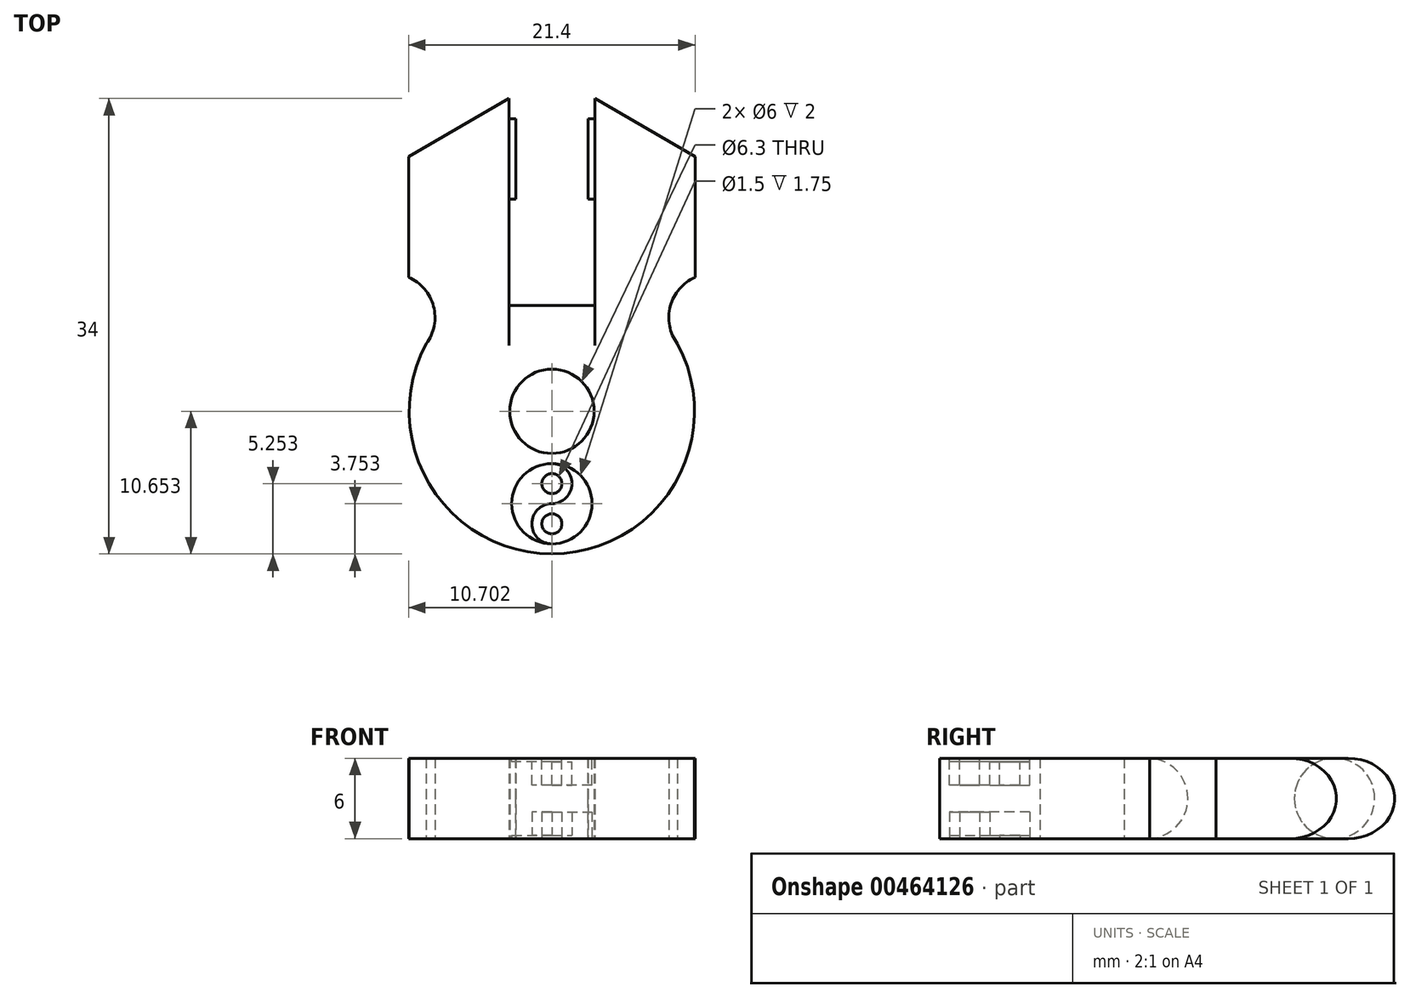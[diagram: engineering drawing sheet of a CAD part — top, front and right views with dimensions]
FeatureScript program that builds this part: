
annotation { "Feature Type Name" : "Feature", "Feature Type Description" : "" }
export const myFeature = defineFeature(function(context is Context, id is Id, definition is map)
    precondition{}
    {
        {
            var Q0;
            Q0=qCreatedBy(makeId("Top.planeOp"),FACE);
            var sketch = newSketch(context, id + "F0", { "sketchPlane" : qUnion([Q0])});
            skCircle(sketch, "E0", {"center": v(-10.56, -6.9) * mm, "radius": 10.65 * mm});
            skCircle(sketch, "E1", {"center": v(-10.56, -6.9) * mm, "radius": 3.15 * mm});
            skLineSegment(sketch, "E2", {"start": v(-10.56, -6.9) * mm, "end": v(-10.56, 3.74) * mm});
            skLineSegment(sketch, "E3", {"start": v(-13.76, 1.2) * mm, "end": v(-13.76, 16.44) * mm});
            skLineSegment(sketch, "E4", {"start": v(-7.36, 1.2) * mm, "end": v(-7.36, 16.44) * mm});
            skLineSegment(sketch, "E5", {"start": v(-7.36, 16.44) * mm, "end": v(0.14, 12.1) * mm});
            skLineSegment(sketch, "E6", {"start": v(-13.76, 16.44) * mm, "end": v(-21.26, 12.1) * mm});
            skLineSegment(sketch, "E7", {"start": v(-21.26, 12.1) * mm, "end": v(-21.26, 3.1) * mm});
            skLineSegment(sketch, "E8", {"start": v(0.14, 12.1) * mm, "end": v(0.14, 3.1) * mm});
            skLineSegment(sketch, "E9", {"start": v(-21.26, 12.1) * mm, "end": v(-21.26, 16.44) * mm});
            skLineSegment(sketch, "E10", {"start": v(-21.26, 16.44) * mm, "end": v(-13.76, 16.44) * mm});
            skArc(sketch, "E11", {"start": v(-19.94, -1.86) * mm, "mid": v(-19.4, 0.93) * mm, "end": v(-21.26, 3.1) * mm});
            skArc(sketch, "E12", {"start": v(0.14, 3.1) * mm, "mid": v(-1.72, 0.93) * mm, "end": v(-1.18, -1.86) * mm});
            skLineSegment(sketch, "E13", {"start": v(-13.76, 1.2) * mm, "end": v(-13.76, 1) * mm});
            skLineSegment(sketch, "E14", {"start": v(-13.76, 1) * mm, "end": v(-7.36, 1) * mm});
            skLineSegment(sketch, "E15", {"start": v(-7.36, 1) * mm, "end": v(-7.36, 1.2) * mm});
            skSolve(sketch);
        }
        {
            var Q0;
            {var subQ0=sQuery(id+"F0.wireOp",EDGE,"E6");Q0=makeQuery(id+"F0.imprint","IMPRINT",FACE,{"disambiguationData":[TD([[makeQuery(id+"F0.imprint","IMPRINT",EDGE,{"derivedFrom":subQ0}),1.0]])]});}
            var Q1;
            Q1=makeQuery(id+"F0.imprint","IMPRINT",FACE,{"disambiguationData":[TD([[makeQuery(id+"F0.imprint","IMPRINT",EDGE,{"derivedFrom":sQuery(id+"F0.wireOp",EDGE,"E1")}),-1.0]])]});
            var Q2;
            {var subQ1=sQuery(id+"F0.wireOp",EDGE,"E5");Q2=makeQuery(id+"F0.imprint","IMPRINT",FACE,{"disambiguationData":[TD([[makeQuery(id+"F0.imprint","IMPRINT",EDGE,{"derivedFrom":subQ1}),-1.0]])]});}
            extrude(context, id + "F1", {"entities" : qUnion([Q0, Q1, Q2]), "depth" : 6 * mm});
        }
        {
            var Q0;
            Q0=makeQuery(id+"F1.opExtrude","SWEPT_FACE",FACE,{"disambiguationData":[OSD([sQuery(id+"F0.wireOp",EDGE,"E3")])]});
            var sketch = newSketch(context, id + "F2", { "sketchPlane" : qUnion([Q0])});
            skCircle(sketch, "E16", {"center": v(11.94, 3) * mm, "radius": 3 * mm});
            skSolve(sketch);
        }
        {
            var Q0;
            {var subQ0=sQuery(id+"F2.wireOp",EDGE,"E16");var subQ1=sQuery(id+"F0.wireOp",EDGE,"E3");var subQ2=makeQuery(id+"F2.imprint","INTERSECT",VERTEX,{"derivedFrom":[makeQuery(id+"F1.opExtrude","CAP_EDGE",EDGE,{"disambiguationData":[OSD([subQ1])],"isStart":true}),subQ0]});Q0=makeQuery(id+"F2.imprint","IMPRINT",FACE,{"disambiguationData":[TD([[makeQuery(id+"F2.imprint","IMPRINT",EDGE,{"disambiguationData":[TD([[subQ2,1.0]])],"derivedFrom":subQ0}),1.0]])]});}
            extrude(context, id + "F3", {"entities" : qUnion([Q0]), "operationType" : NewBodyOperationType.ADD, "depth" : .5 * mm});
        }
        {
            var Q0;
            Q0=makeQuery(id+"F1.opExtrude","SWEPT_FACE",FACE,{"disambiguationData":[OSD([sQuery(id+"F0.wireOp",EDGE,"E4")])]});
            var sketch = newSketch(context, id + "F4", { "sketchPlane" : qUnion([Q0])});
            skCircle(sketch, "E17", {"center": v(-11.94, 3) * mm, "radius": 3 * mm});
            skSolve(sketch);
        }
        {
            var Q0;
            {var subQ0=sQuery(id+"F4.wireOp",EDGE,"E17");var subQ1=sQuery(id+"F0.wireOp",EDGE,"E4");var subQ2=makeQuery(id+"F4.imprint","INTERSECT",VERTEX,{"derivedFrom":[makeQuery(id+"F1.opExtrude","CAP_EDGE",EDGE,{"disambiguationData":[OSD([subQ1])],"isStart":true}),subQ0]});Q0=makeQuery(id+"F4.imprint","IMPRINT",FACE,{"disambiguationData":[TD([[makeQuery(id+"F4.imprint","IMPRINT",EDGE,{"disambiguationData":[TD([[subQ2,1.0]])],"derivedFrom":subQ0}),1.0]])]});}
            extrude(context, id + "F5", {"entities" : qUnion([Q0]), "operationType" : NewBodyOperationType.ADD, "depth" : .5 * mm});
        }
        {
            var Q0;
            Q0=makeQuery(id+"F1.opExtrude","CAP_EDGE",EDGE,{"disambiguationData":[OSD([sQuery(id+"F0.wireOp",EDGE,"E14")])],"isStart":true});
            var Q1;
            Q1=makeQuery(id+"F1.opExtrude","CAP_EDGE",EDGE,{"disambiguationData":[OSD([sQuery(id+"F0.wireOp",EDGE,"E14")])],"isStart":false});
            fillet(context, id + "F6", {"entities" : qUnion([Q0, Q1]), "radius" : 3 * mm, "tangentPropagation" : true, "allowEdgeOverflow" : false});
        }
        {
            var Q0;
            Q0=makeQuery(id+"F1.opExtrude","CAP_EDGE",EDGE,{"disambiguationData":[OSD([sQuery(id+"F0.wireOp",EDGE,"E5")])],"isStart":false});
            var Q1;
            Q1=makeQuery(id+"F1.opExtrude","CAP_EDGE",EDGE,{"disambiguationData":[OSD([sQuery(id+"F0.wireOp",EDGE,"E5")])],"isStart":true});
            var Q2;
            Q2=makeQuery(id+"F1.opExtrude","CAP_EDGE",EDGE,{"disambiguationData":[OSD([sQuery(id+"F0.wireOp",EDGE,"E6")])],"isStart":false});
            var Q3;
            Q3=makeQuery(id+"F1.opExtrude","CAP_EDGE",EDGE,{"disambiguationData":[OSD([sQuery(id+"F0.wireOp",EDGE,"E6")])],"isStart":true});
            fillet(context, id + "F7", {"entities" : qUnion([Q0, Q1, Q2, Q3]), "radius" : 3 * mm, "tangentPropagation" : true, "allowEdgeOverflow" : false});
        }
        {
            var Q0;
            Q0=makeQuery(id+"F1.opExtrude","CAP_FACE",FACE,{"disambiguationData":[OSD([sQuery(id+"F0.wireOp",EDGE,"E0"),sQuery(id+"F0.wireOp",EDGE,"E1"),sQuery(id+"F0.wireOp",EDGE,"E3"),sQuery(id+"F0.wireOp",EDGE,"E4"),sQuery(id+"F0.wireOp",EDGE,"E5"),sQuery(id+"F0.wireOp",EDGE,"E6"),sQuery(id+"F0.wireOp",EDGE,"E7"),sQuery(id+"F0.wireOp",EDGE,"E8"),sQuery(id+"F0.wireOp",EDGE,"E11"),sQuery(id+"F0.wireOp",EDGE,"E12"),sQuery(id+"F0.wireOp",EDGE,"E13"),sQuery(id+"F0.wireOp",EDGE,"E14"),sQuery(id+"F0.wireOp",EDGE,"E15")])],"isStart":false});
            var sketch = newSketch(context, id + "F8", { "sketchPlane" : qUnion([Q0])});
            skCircle(sketch, "E18", {"center": v(-10.56, -6.9) * mm, "radius": 3.15 * mm});
            skLineSegment(sketch, "E19", {"start": v(-10.56, -6.9) * mm, "end": v(-10.56, -17.56) * mm});
            skCircle(sketch, "E20", {"center": v(-10.56, -13.8) * mm, "radius": 3 * mm});
            skArc(sketch, "E21", {"start": v(-10.56, -13.8) * mm, "mid": v(-9.06, -12.3) * mm, "end": v(-10.56, -10.8) * mm});
            skArc(sketch, "E22", {"start": v(-10.56, -13.8) * mm, "mid": v(-12.06, -15.3) * mm, "end": v(-10.56, -16.8) * mm});
            skCircle(sketch, "E23", {"center": v(-10.56, -12.3) * mm, "radius": 0.75 * mm});
            skCircle(sketch, "E24", {"center": v(-10.56, -15.3) * mm, "radius": 0.75 * mm});
            skSolve(sketch);
        }
        {
            var Q0;
            {var subQ0=sQuery(id+"F8.wireOp",EDGE,"E22");Q0=makeQuery(id+"F8.imprint","IMPRINT",FACE,{"disambiguationData":[TD([[makeQuery(id+"F8.imprint","IMPRINT",EDGE,{"derivedFrom":subQ0}),1.0]])]});}
            var Q1;
            {var subQ0=sQuery(id+"F8.wireOp",EDGE,"E21");Q1=makeQuery(id+"F8.imprint","IMPRINT",FACE,{"disambiguationData":[TD([[makeQuery(id+"F8.imprint","IMPRINT",EDGE,{"derivedFrom":subQ0}),-1.0]])]});}
            var Q2;
            {var subQ0=sQuery(id+"F8.wireOp",EDGE,"E23");var subQ1=sQuery(id+"F8.wireOp",EDGE,"E19");var subQ2=makeQuery(id+"F8.imprint","INTERSECT",VERTEX,{"disambiguationData":[OD(0.0)],"derivedFrom":[subQ1,subQ0]});Q2=makeQuery(id+"F8.imprint","IMPRINT",FACE,{"disambiguationData":[TD([[makeQuery(id+"F8.imprint","IMPRINT",EDGE,{"disambiguationData":[TD([[subQ2,-1.0]])],"derivedFrom":subQ1}),-1.0]])]});}
            var Q3;
            {var subQ0=sQuery(id+"F8.wireOp",EDGE,"E23");var subQ1=sQuery(id+"F8.wireOp",EDGE,"E19");var subQ2=makeQuery(id+"F8.imprint","INTERSECT",VERTEX,{"disambiguationData":[OD(0.0)],"derivedFrom":[subQ1,subQ0]});Q3=makeQuery(id+"F8.imprint","IMPRINT",FACE,{"disambiguationData":[TD([[makeQuery(id+"F8.imprint","IMPRINT",EDGE,{"disambiguationData":[TD([[subQ2,-1.0]])],"derivedFrom":subQ1}),1.0]])]});}
            extrude(context, id + "F9", {"entities" : qUnion([Q0, Q1, Q2, Q3]), "operationType" : NewBodyOperationType.REMOVE, "oppositeDirection" : true, "depth" : 2 * mm, "offsetDistance" : 25 * mm});
        }
        {
            var Q0;
            {var subQ0=sQuery(id+"F8.wireOp",EDGE,"E22");Q0=makeQuery(id+"F8.imprint","IMPRINT",FACE,{"disambiguationData":[TD([[makeQuery(id+"F8.imprint","IMPRINT",EDGE,{"derivedFrom":subQ0}),-1.0]])]});}
            var Q1;
            {var subQ0=sQuery(id+"F8.wireOp",EDGE,"E21");Q1=makeQuery(id+"F8.imprint","IMPRINT",FACE,{"disambiguationData":[TD([[makeQuery(id+"F8.imprint","IMPRINT",EDGE,{"derivedFrom":subQ0}),1.0]])]});}
            var Q2;
            {var subQ0=sQuery(id+"F8.wireOp",EDGE,"E24");var subQ1=sQuery(id+"F8.wireOp",EDGE,"E19");var subQ2=makeQuery(id+"F8.imprint","INTERSECT",VERTEX,{"disambiguationData":[OD(0.0)],"derivedFrom":[subQ1,subQ0]});Q2=makeQuery(id+"F8.imprint","IMPRINT",FACE,{"disambiguationData":[TD([[makeQuery(id+"F8.imprint","IMPRINT",EDGE,{"disambiguationData":[TD([[subQ2,-1.0]])],"derivedFrom":subQ1}),1.0]])]});}
            var Q3;
            {var subQ0=sQuery(id+"F8.wireOp",EDGE,"E24");var subQ1=sQuery(id+"F8.wireOp",EDGE,"E19");var subQ2=makeQuery(id+"F8.imprint","INTERSECT",VERTEX,{"disambiguationData":[OD(0.0)],"derivedFrom":[subQ1,subQ0]});Q3=makeQuery(id+"F8.imprint","IMPRINT",FACE,{"disambiguationData":[TD([[makeQuery(id+"F8.imprint","IMPRINT",EDGE,{"disambiguationData":[TD([[subQ2,-1.0]])],"derivedFrom":subQ1}),-1.0]])]});}
            extrude(context, id + "F10", {"entities" : qUnion([Q0, Q1, Q2, Q3]), "operationType" : NewBodyOperationType.REMOVE, "oppositeDirection" : true, "depth" : 0.25 * mm, "offsetDistance" : 25 * mm});
        }
        {
            var Q0;
            Q0=makeQuery(id+"F1.opExtrude","CAP_FACE",FACE,{"disambiguationData":[OSD([sQuery(id+"F0.wireOp",EDGE,"E0"),sQuery(id+"F0.wireOp",EDGE,"E1"),sQuery(id+"F0.wireOp",EDGE,"E3"),sQuery(id+"F0.wireOp",EDGE,"E4"),sQuery(id+"F0.wireOp",EDGE,"E5"),sQuery(id+"F0.wireOp",EDGE,"E6"),sQuery(id+"F0.wireOp",EDGE,"E7"),sQuery(id+"F0.wireOp",EDGE,"E8"),sQuery(id+"F0.wireOp",EDGE,"E11"),sQuery(id+"F0.wireOp",EDGE,"E12"),sQuery(id+"F0.wireOp",EDGE,"E13"),sQuery(id+"F0.wireOp",EDGE,"E14"),sQuery(id+"F0.wireOp",EDGE,"E15")])],"isStart":true});
            var sketch = newSketch(context, id + "F11", { "sketchPlane" : qUnion([Q0])});
            skCircle(sketch, "E25.0", {"center": v(-10.56, 13.8) * mm, "radius": 3 * mm});
            skArc(sketch, "E26.0", {"start": v(-10.56, 13.8) * mm, "mid": v(-12.06, 15.3) * mm, "end": v(-10.56, 16.8) * mm});
            skCircle(sketch, "E27.0", {"center": v(-10.56, 15.3) * mm, "radius": 0.75 * mm});
            skArc(sketch, "E28.0", {"start": v(-10.56, 13.8) * mm, "mid": v(-9.06, 12.3) * mm, "end": v(-10.56, 10.8) * mm});
            skCircle(sketch, "E29.0", {"center": v(-10.56, 12.3) * mm, "radius": 0.75 * mm});
            skSolve(sketch);
        }
        {
            var Q0;
            {var subQ0=sQuery(id+"F11.wireOp",EDGE,"E26.0");Q0=makeQuery(id+"F11.imprint","IMPRINT",FACE,{"disambiguationData":[TD([[makeQuery(id+"F11.imprint","IMPRINT",EDGE,{"derivedFrom":subQ0}),1.0]])]});}
            var Q1;
            Q1=makeQuery(id+"F11.imprint","IMPRINT",FACE,{"disambiguationData":[TD([[makeQuery(id+"F11.imprint","IMPRINT",EDGE,{"derivedFrom":sQuery(id+"F11.wireOp",EDGE,"E27.0")}),-1.0]])]});
            extrude(context, id + "F12", {"entities" : qUnion([Q0, Q1]), "operationType" : NewBodyOperationType.REMOVE, "oppositeDirection" : true, "depth" : 2 * mm, "offsetDistance" : 25 * mm});
        }
        {
            var Q0;
            {var subQ0=sQuery(id+"F11.wireOp",EDGE,"E26.0");Q0=makeQuery(id+"F11.imprint","IMPRINT",FACE,{"disambiguationData":[TD([[makeQuery(id+"F11.imprint","IMPRINT",EDGE,{"derivedFrom":subQ0}),-1.0]])]});}
            var Q1;
            Q1=makeQuery(id+"F11.imprint","IMPRINT",FACE,{"disambiguationData":[TD([[makeQuery(id+"F11.imprint","IMPRINT",EDGE,{"derivedFrom":sQuery(id+"F11.wireOp",EDGE,"E29.0")}),-1.0]])]});
            extrude(context, id + "F13", {"entities" : qUnion([Q0, Q1]), "operationType" : NewBodyOperationType.REMOVE, "oppositeDirection" : true, "depth" : 0.25 * mm, "offsetDistance" : 25 * mm});
        }
    });
